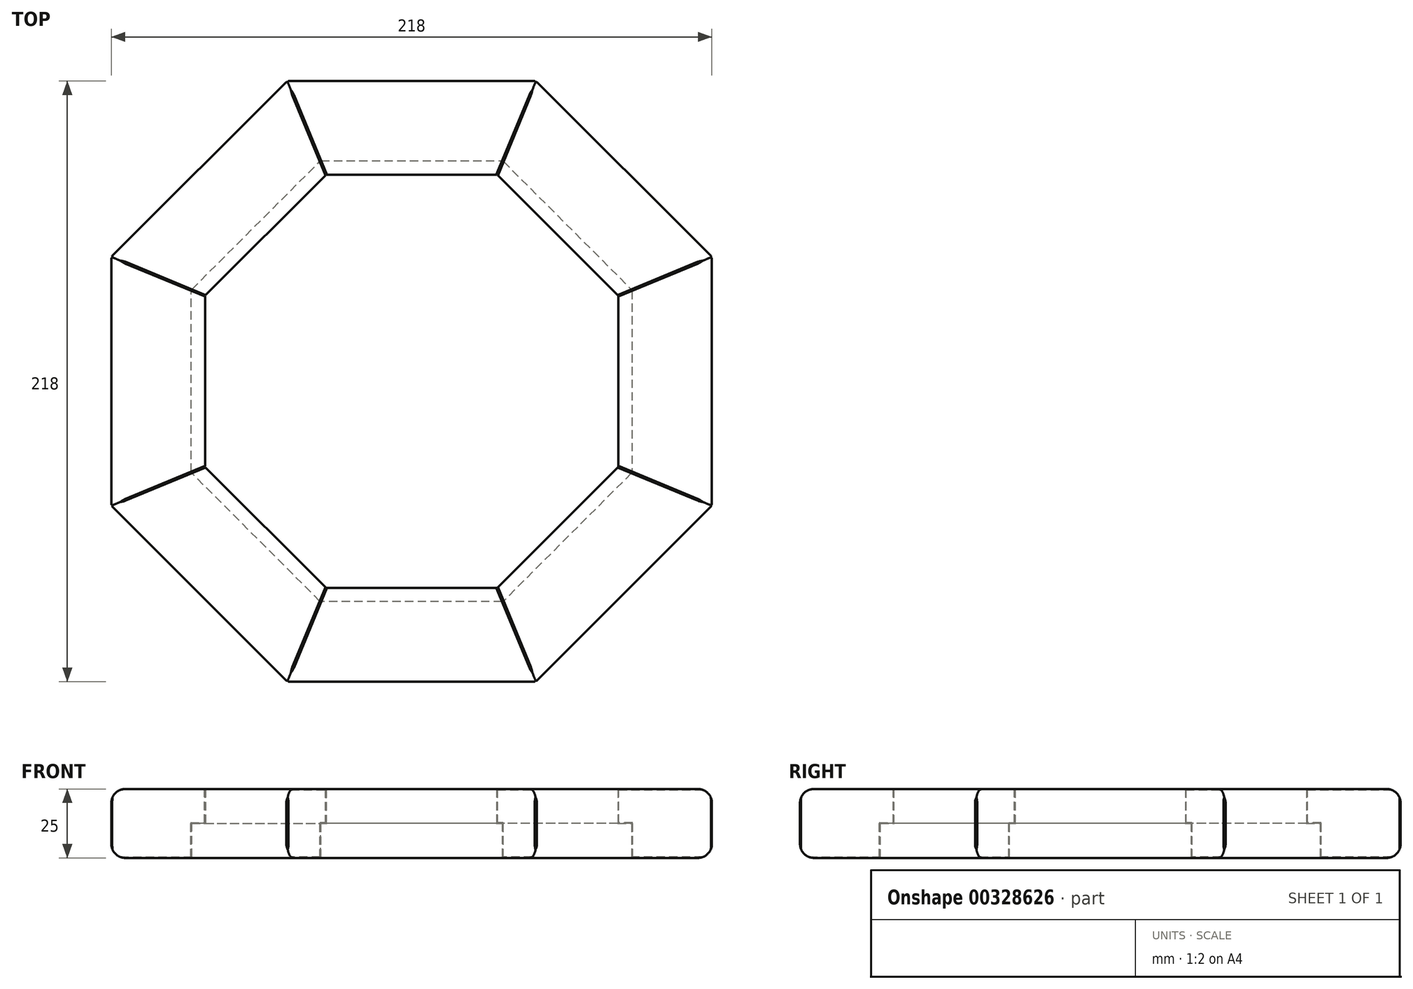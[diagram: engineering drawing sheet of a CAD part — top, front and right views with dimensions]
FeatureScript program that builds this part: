
annotation { "Feature Type Name" : "Feature", "Feature Type Description" : "" }
export const myFeature = defineFeature(function(context is Context, id is Id, definition is map)
    precondition{}
    {
        {
            var Q0;
            Q0=qCreatedBy(makeId("Top.planeOp"),FACE);
            var sketch = newSketch(context, id + "F0", { "sketchPlane" : qUnion([Q0])});
            skLineSegment(sketch, "E0", {"start": v(0, 0) * mm, "end": v(0, -75) * mm, "construction": true});
            skLineSegment(sketch, "E1", {"start": v(0, 0) * mm, "end": v(-31.07, -75) * mm, "construction": true});
            skLineSegment(sketch, "E2", {"start": v(0, 0) * mm, "end": v(31.07, -75) * mm, "construction": true});
            skLineSegment(sketch, "E3", {"start": v(31.07, -75) * mm, "end": v(0, -75) * mm});
            skLineSegment(sketch, "E4", {"start": v(0, -75) * mm, "end": v(-31.07, -75) * mm});
            skLineSegment(sketch, "E5", {"start": v(-31.07, -75) * mm, "end": v(-45.15, -109) * mm});
            skLineSegment(sketch, "E6", {"start": v(-45.15, -109) * mm, "end": v(45.15, -109) * mm});
            skLineSegment(sketch, "E7", {"start": v(31.07, -75) * mm, "end": v(45.15, -109) * mm});
            skSolve(sketch);
        }
        {
            var Q0;
            Q0=qSketchRegion(id+"F0",true);
            extrude(context, id + "F1", {"entities" : qUnion([Q0]), "oppositeDirection" : true, "depth" : 25 * mm});
        }
        {
            var Q0;
            Q0=makeQuery(id+"F1.opExtrude","CAP_FACE",FACE,{"disambiguationData":[OSD([sQuery(id+"F0.wireOp",EDGE,"E3"),sQuery(id+"F0.wireOp",EDGE,"E4"),sQuery(id+"F0.wireOp",EDGE,"E5"),sQuery(id+"F0.wireOp",EDGE,"E6"),sQuery(id+"F0.wireOp",EDGE,"E7")])],"isStart":false});
            var sketch = newSketch(context, id + "F2", { "sketchPlane" : qUnion([Q0])});
            skLineSegment(sketch, "E8", {"start": v(33.14, 80) * mm, "end": v(-33.14, 80) * mm});
            skLineSegment(sketch, "E9", {"start": v(-33.14, 80) * mm, "end": v(-31.07, 75) * mm});
            skLineSegment(sketch, "E10", {"start": v(-31.07, 75) * mm, "end": v(31.07, 75) * mm});
            skLineSegment(sketch, "E11", {"start": v(31.07, 75) * mm, "end": v(33.14, 80) * mm});
            skSolve(sketch);
        }
        {
            var Q0;
            Q0=qSketchRegion(id+"F2",true);
            extrude(context, id + "F3", {"entities" : qUnion([Q0]), "operationType" : NewBodyOperationType.REMOVE, "oppositeDirection" : true, "depth" : 12.5 * mm});
        }
        {
            var Q0;
            Q0=makeQuery(id+"F1.opExtrude","SWEPT_FACE",FACE,{"disambiguationData":[OSD([sQuery(id+"F0.wireOp",EDGE,"E7")])]});
            var Q1;
            Q1=makeQuery(id+"F1.opExtrude","SWEPT_FACE",FACE,{"disambiguationData":[OSD([sQuery(id+"F0.wireOp",EDGE,"E5")])]});
            chamfer(context, id + "F4", {"entities" : qUnion([Q0, Q1]), "width" : .3 * mm, "tangentPropagation" : true});
        }
        {
            var Q0;
            Q0=makeQuery(id+"F1.opExtrude","CAP_EDGE",EDGE,{"disambiguationData":[OSD([sQuery(id+"F0.wireOp",EDGE,"E6")])],"isStart":false});
            var Q1;
            Q1=makeQuery(id+"F1.opExtrude","CAP_EDGE",EDGE,{"disambiguationData":[OSD([sQuery(id+"F0.wireOp",EDGE,"E6")])],"isStart":true});
            fillet(context, id + "F5", {"entities" : qUnion([Q0, Q1]), "radius" : 5 * mm, "tangentPropagation" : true, "allowEdgeOverflow" : false});
        }
        {
            var Q0;
            Q0=qCreatedBy(makeId("Right.planeOp"),FACE);
            var sketch = newSketch(context, id + "F6", { "sketchPlane" : qUnion([Q0])});
            skLineSegment(sketch, "E12", {"start": v(0, 0) * mm, "end": v(0, 46.88) * mm, "construction": true});
            skSolve(sketch);
        }
        {
            var Q0;
            Q0=makeQuery(id+"F1.opExtrude","SWEPT_BODY",BODY,{"disambiguationData":[OSD([sQuery(id+"F0.wireOp",EDGE,"E3"),sQuery(id+"F0.wireOp",EDGE,"E4"),sQuery(id+"F0.wireOp",EDGE,"E5"),sQuery(id+"F0.wireOp",EDGE,"E6"),sQuery(id+"F0.wireOp",EDGE,"E7")])]});
            var Q1;
            Q1=sQuery(id+"F6.wireOp",EDGE,"E12");
            circularPattern(context, id + "F7", {"operationType" : NewBodyOperationType.ADD, "entities" : qUnion([Q0]), "axis" : qUnion([Q1]), "angle" : 360 * degree, "instanceCount" : 8, "equalSpace" : true});
        }
    });
